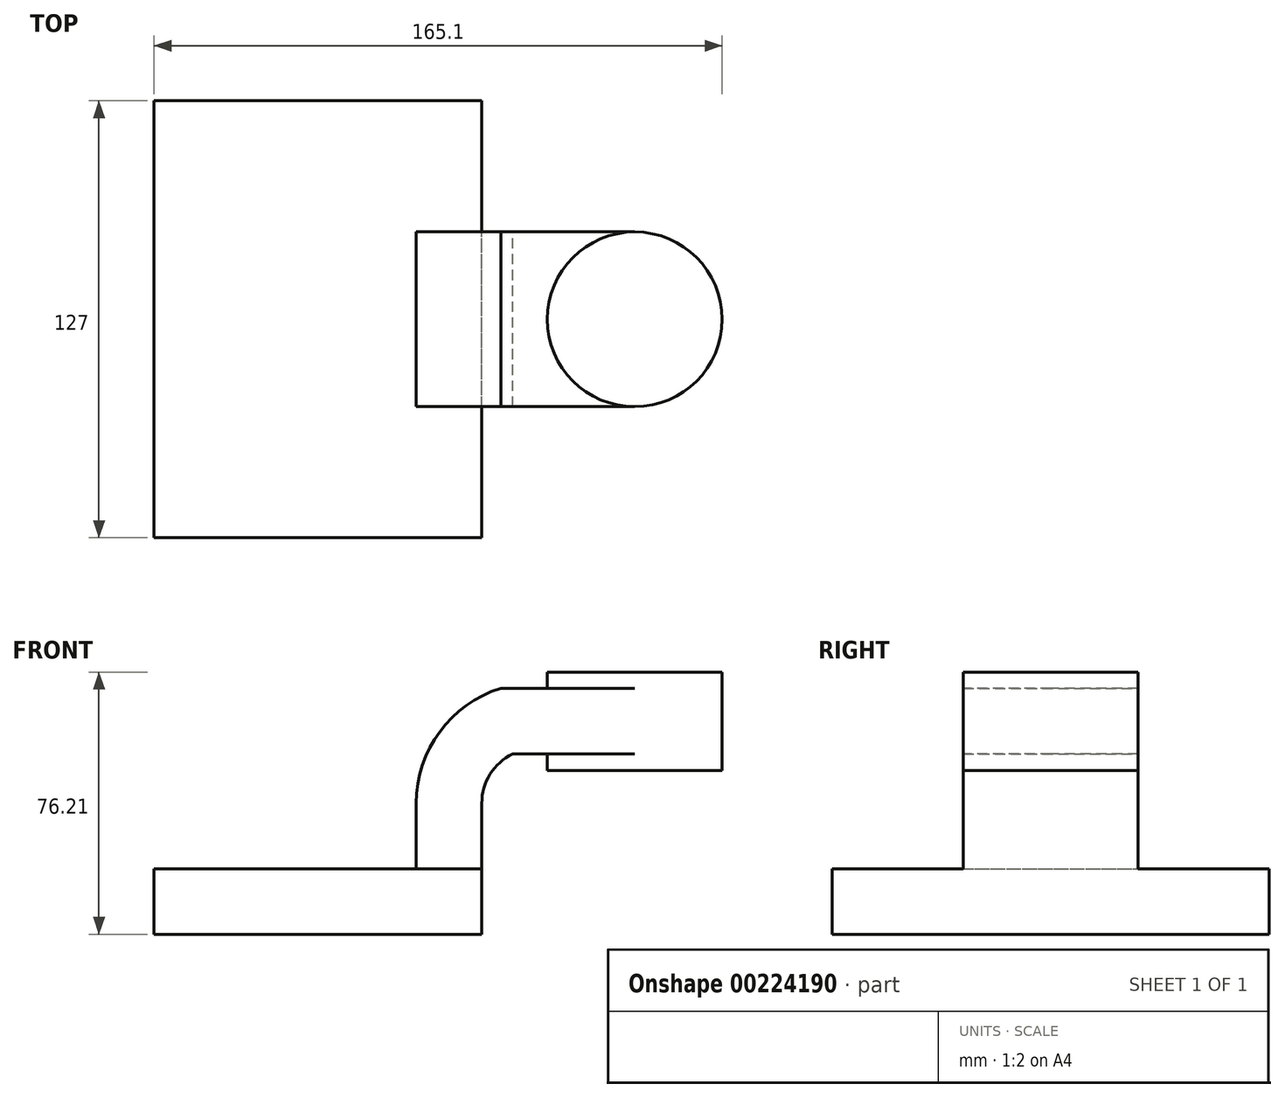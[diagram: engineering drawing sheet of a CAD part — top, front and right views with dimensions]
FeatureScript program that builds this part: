
annotation { "Feature Type Name" : "Feature", "Feature Type Description" : "" }
export const myFeature = defineFeature(function(context is Context, id is Id, definition is map)
    precondition{}
    {
        {
            var Q0;
            Q0=qCreatedBy(makeId("Front.planeOp"),FACE);
            var sketch = newSketch(context, id + "F0", { "sketchPlane" : qUnion([Q0])});
            skLineSegment(sketch, "E0.bottom", {"start": v(47.63, -9.53) * mm, "end": v(-47.63, -9.53) * mm});
            skLineSegment(sketch, "E0.top", {"start": v(47.62, 9.52) * mm, "end": v(-47.63, 9.52) * mm});
            skLineSegment(sketch, "E0.left", {"start": v(47.63, -9.52) * mm, "end": v(47.63, 9.53) * mm});
            skLineSegment(sketch, "E0.right", {"start": v(-47.63, -9.53) * mm, "end": v(-47.63, 9.53) * mm});
            skPoint(sketch, "E0.middle", {"position": v(0, 0) * mm});
            skLineSegment(sketch, "E1.bottom", {"start": v(117.47, 38.1) * mm, "end": v(66.67, 38.1) * mm});
            skLineSegment(sketch, "E1.top", {"start": v(117.47, 66.67) * mm, "end": v(66.67, 66.67) * mm});
            skLineSegment(sketch, "E1.left", {"start": v(117.47, 38.1) * mm, "end": v(117.47, 66.68) * mm});
            skLineSegment(sketch, "E1.right", {"start": v(66.67, 38.1) * mm, "end": v(66.67, 66.68) * mm});
            skPoint(sketch, "E1.middle", {"position": v(92.08, 52.39) * mm});
            skLineSegment(sketch, "E2", {"start": v(47.63, 9.53) * mm, "end": v(47.63, 28.58) * mm});
            skArc(sketch, "E3", {"start": v(47.62, 28.58) * mm, "mid": v(50.06, 37.02) * mm, "end": v(56.6, 42.88) * mm});
            skLineSegment(sketch, "E4", {"start": v(56.6, 42.88) * mm, "end": v(92.07, 42.88) * mm});
            skLineSegment(sketch, "E5.0", {"start": v(53.13, 61.93) * mm, "end": v(92.08, 61.93) * mm});
            skArc(sketch, "E5.1", {"start": v(28.58, 28.58) * mm, "mid": v(35.38, 49.28) * mm, "end": v(53.13, 61.93) * mm});
            skLineSegment(sketch, "E5.2", {"start": v(28.58, 9.53) * mm, "end": v(28.58, 28.58) * mm});
            skLineSegment(sketch, "E6", {"start": v(92.08, 38.1) * mm, "end": v(92.08, 66.68) * mm});
            skFitSpline(sketch, "E7", {"points": [v(-47.63, 9.53) * mm, v(53.13, 61.93) * mm], "startDerivative": vector(-0.28, 119.22) * mm, "endDerivative": vector(62.54, 19.45) * mm});
            skSolve(sketch);
        }
        {
            var Q0;
            Q0=makeQuery(id+"F0.imprint","IMPRINT",FACE,{"disambiguationData":[TD([[makeQuery(id+"F0.imprint","IMPRINT",EDGE,{"derivedFrom":sQuery(id+"F0.wireOp",EDGE,"E0.bottom")}),-1.0]])]});
            extrude(context, id + "F1", {"entities" : qUnion([Q0]), "endBound" : BoundingType.SYMMETRIC, "depth" : 127 * mm});
        }
        {
            var Q0;
            {var subQ2=sQuery(id+"F0.wireOp",EDGE,"E2");Q0=makeQuery(id+"F0.imprint","IMPRINT",FACE,{"disambiguationData":[TD([[makeQuery(id+"F0.imprint","IMPRINT",EDGE,{"derivedFrom":subQ2}),1.0]])]});}
            var Q1;
            {var subQ0=sQuery(id+"F0.wireOp",EDGE,"E4");var subQ1=sQuery(id+"F0.wireOp",EDGE,"E1.right");var subQ2=makeQuery(id+"F0.imprint","INTERSECT",VERTEX,{"derivedFrom":[subQ1,subQ0]});Q1=makeQuery(id+"F0.imprint","IMPRINT",FACE,{"disambiguationData":[TD([[makeQuery(id+"F0.imprint","IMPRINT",EDGE,{"disambiguationData":[TD([[subQ2,-1.0]])],"derivedFrom":subQ1}),-1.0]])]});}
            extrude(context, id + "F2", {"entities" : qUnion([Q0, Q1]), "operationType" : NewBodyOperationType.ADD, "endBound" : BoundingType.SYMMETRIC, "depth" : 50.8 * mm});
        }
        {
            var Q0;
            Q0=makeQuery(id+"F0.imprint","IMPRINT",FACE,{"disambiguationData":[TD([[makeQuery(id+"F0.imprint","IMPRINT",EDGE,{"derivedFrom":sQuery(id+"F0.wireOp",EDGE,"E5.1")}),1.0]])]});
            extrude(context, id + "F3", {"entities" : qUnion([Q0]), "operationType" : NewBodyOperationType.ADD, "endBound" : BoundingType.SYMMETRIC, "depth" : 15.88 * mm});
        }
        {
            var Q0;
            {var subQ0=sQuery(id+"F0.wireOp",EDGE,"E1.left");Q0=makeQuery(id+"F0.imprint","IMPRINT",FACE,{"disambiguationData":[TD([[makeQuery(id+"F0.imprint","IMPRINT",EDGE,{"derivedFrom":subQ0}),1.0]])]});}
            var Q1;
            Q1=sQuery(id+"F0.wireOp",EDGE,"E6");
            revolve(context, id + "F4", {"operationType" : NewBodyOperationType.ADD, "entities" : qUnion([Q0]), "axis" : qUnion([Q1]), "revolveType" : RevolveType.FULL});
        }
    });
